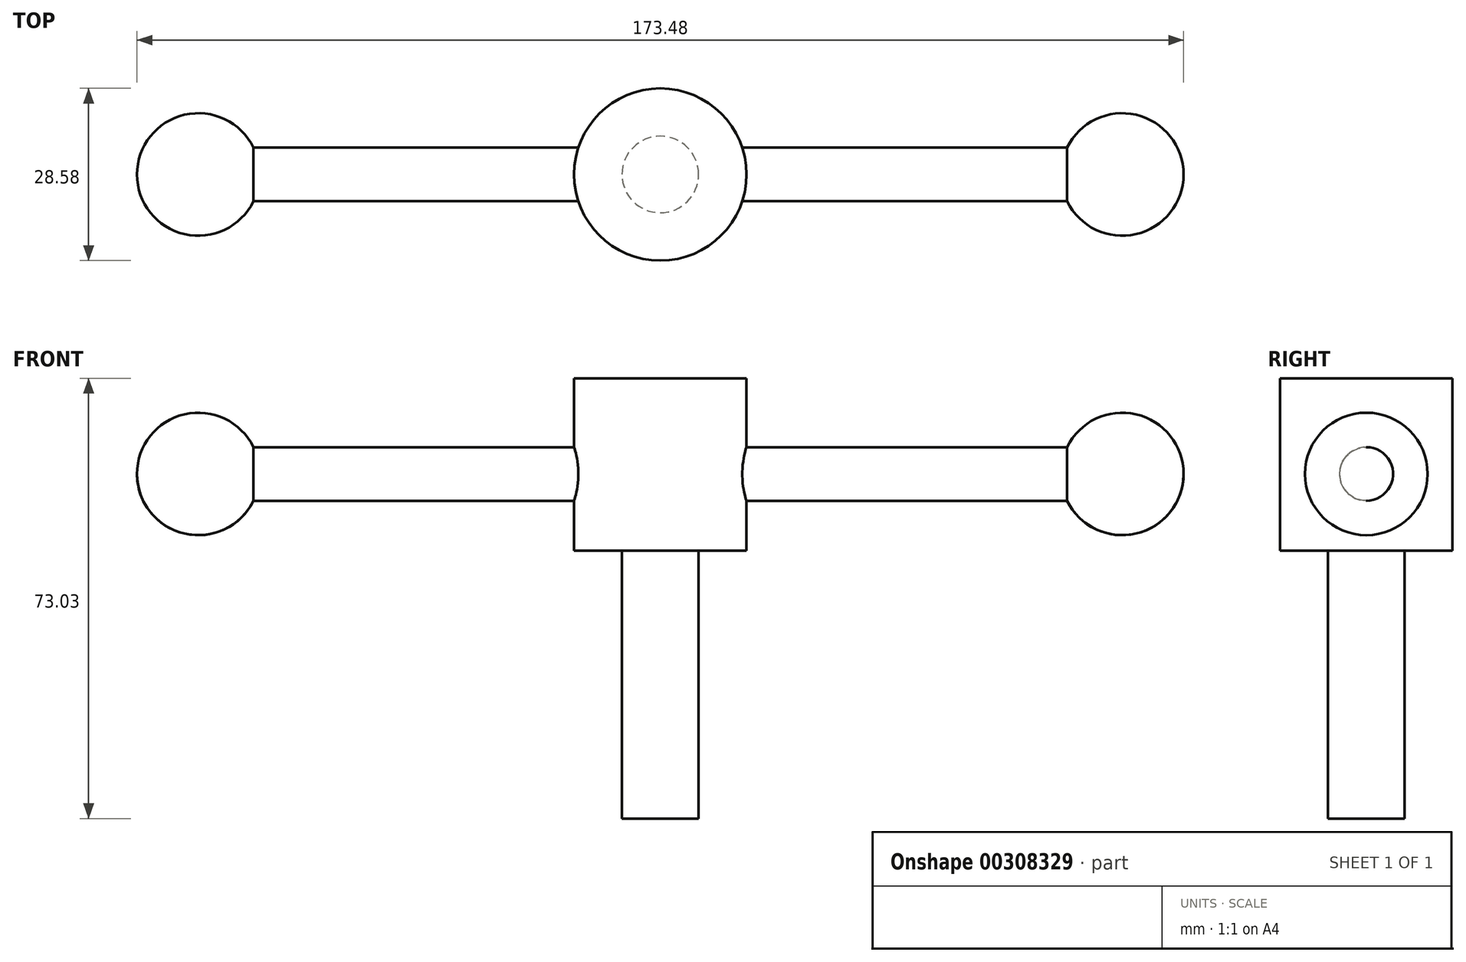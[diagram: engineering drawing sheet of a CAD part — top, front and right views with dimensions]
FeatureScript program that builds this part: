
annotation { "Feature Type Name" : "Feature", "Feature Type Description" : "" }
export const myFeature = defineFeature(function(context is Context, id is Id, definition is map)
    precondition{}
    {
        {
            var Q0;
            Q0=qCreatedBy(makeId("Top.planeOp"),FACE);
            var sketch = newSketch(context, id + "F0", { "sketchPlane" : qUnion([Q0])});
            skCircle(sketch, "E0", {"center": v(0, 0) * mm, "radius": 14.29 * mm});
            skSolve(sketch);
        }
        {
            var Q0;
            Q0 = qSketchRegion(id + "F0", true);
            extrude(context, id + "F1", {"entities" : qUnion([Q0]), "endBound" : BoundingType.SYMMETRIC, "depth" : 28.57 * mm});
        }
        {
            var Q0;
            Q0=makeQuery(id+"F1.opExtrude","CAP_FACE",FACE,{"disambiguationData":[OSD([sQuery(id+"F0.wireOp",EDGE,"E0")])],"isStart":true});
            var sketch = newSketch(context, id + "F2", { "sketchPlane" : qUnion([Q0])});
            skCircle(sketch, "E1", {"center": v(0, 0) * mm, "radius": 6.35 * mm});
            skSolve(sketch);
        }
        {
            var Q0;
            Q0 = qSketchRegion(id + "F2", true);
            extrude(context, id + "F3", {"entities" : qUnion([Q0]), "operationType" : NewBodyOperationType.ADD, "depth" : 44.45 * mm});
        }
        {
            var Q0;
            Q0=qCreatedBy(makeId("Right.planeOp"),FACE);
            var sketch = newSketch(context, id + "F4", { "sketchPlane" : qUnion([Q0])});
            skCircle(sketch, "E2", {"center": v(0, -1.59) * mm, "radius": 4.45 * mm});
            skSolve(sketch);
        }
        {
            var Q0;
            Q0 = qSketchRegion(id + "F4", true);
            extrude(context, id + "F5", {"entities" : qUnion([Q0]), "operationType" : NewBodyOperationType.ADD, "endBound" : BoundingType.SYMMETRIC, "depth" : 152.4 * mm});
        }
        {
            var Q0;
            Q0=qCreatedBy(makeId("Front.planeOp"),FACE);
            var sketch = newSketch(context, id + "F6", { "sketchPlane" : qUnion([Q0])});
            skLineSegment(sketch, "E3", {"start": v(0, 36.85) * mm, "end": v(0, -70.53) * mm, "construction": true});
            skLineSegment(sketch, "E4", {"start": v(-76.58, -1.59) * mm, "end": v(-42.9, -1.59) * mm, "construction": true});
            skArc(sketch, "E5", {"start": v(-66.42, -1.59) * mm, "mid": v(-76.58, 8.57) * mm, "end": v(-86.74, -1.59) * mm});
            skLineSegment(sketch, "E6", {"start": v(-66.42, -1.59) * mm, "end": v(-86.74, -1.59) * mm});
            skArc(sketch, "E7.MirrorCS", {"start": v(66.42, -1.59) * mm, "mid": v(76.58, 8.57) * mm, "end": v(86.74, -1.59) * mm});
            skLineSegment(sketch, "E8.MirrorCS", {"start": v(66.42, -1.59) * mm, "end": v(86.74, -1.59) * mm});
            skSolve(sketch);
        }
        {
            var Q0;
            Q0 = qSketchRegion(id + "F6", true);
            var Q1;
            Q1=sQuery(id+"F6.wireOp",EDGE,"E6");
            revolve(context, id + "F7", {"operationType" : NewBodyOperationType.ADD, "entities" : qUnion([Q0]), "axis" : qUnion([Q1]), "revolveType" : RevolveType.FULL});
        }
    });
